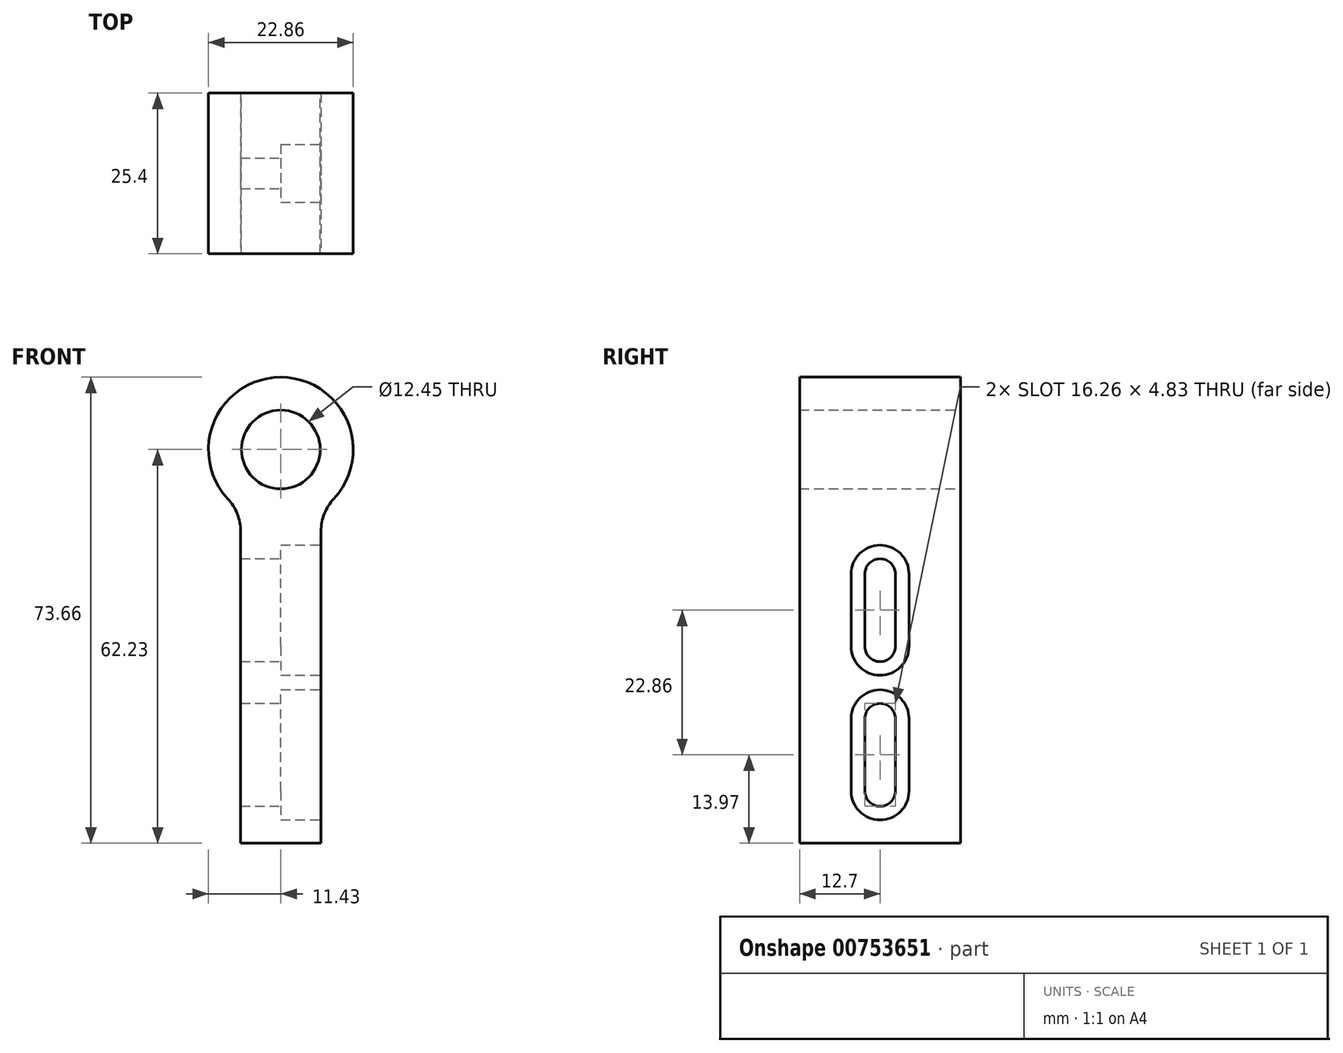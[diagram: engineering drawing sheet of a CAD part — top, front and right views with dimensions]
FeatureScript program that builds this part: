
annotation { "Feature Type Name" : "Feature", "Feature Type Description" : "" }
export const myFeature = defineFeature(function(context is Context, id is Id, definition is map)
    precondition{}
    {
        {
            var Q0;
            Q0=qCreatedBy(makeId("Front.planeOp"),FACE);
            var sketch = newSketch(context, id + "F0", { "sketchPlane" : qUnion([Q0])});
            skLineSegment(sketch, "E0", {"start": v(-6.35, 0) * mm, "end": v(6.35, 0) * mm});
            skLineSegment(sketch, "E1", {"start": v(6.35, 0) * mm, "end": v(6.35, 52.73) * mm});
            skLineSegment(sketch, "E2", {"start": v(-6.35, 52.73) * mm, "end": v(-6.35, 0) * mm});
            skCircle(sketch, "E3", {"center": v(0, 62.23) * mm, "radius": 6.22 * mm});
            skArc(sketch, "E4", {"start": v(6.35, 52.73) * mm, "mid": v(0, 73.66) * mm, "end": v(-6.35, 52.73) * mm});
            skSolve(sketch);
        }
        {
            var Q0;
            Q0=qSketchRegion(id+"F0",true);
            extrude(context, id + "F1", {"entities" : qUnion([Q0]), "endBound" : BoundingType.SYMMETRIC, "depth" : 25.4 * mm, "offsetDistance" : 25.4 * mm});
        }
        {
            var Q0;
            Q0=makeQuery(id+"F1.opExtrude","SWEPT_FACE",FACE,{"disambiguationData":[OSD([sQuery(id+"F0.wireOp",EDGE,"E1")])]});
            var sketch = newSketch(context, id + "F2", { "sketchPlane" : qUnion([Q0])});
            skCircle(sketch, "E5", {"center": v(0, 36.83) * mm, "radius": 2.41 * mm});
            skCircle(sketch, "E6", {"center": v(0, 13.97) * mm, "radius": 2.41 * mm});
            skSolve(sketch);
        }
        {
            var Q0;
            Q0=makeQuery(id+"F1.opExtrude","SWEPT_EDGE",EDGE,{"disambiguationData":[OSD([sQuery(id+"F0.wireOp",EDGE,"E2"),sQuery(id+"F0.wireOp",EDGE,"E4")])]});
            var Q1;
            {var subQ0=sQuery(id+"F0.wireOp",EDGE,"E2");Q1=makeQuery(id+"FnLNvNWXCwf8mwK_1.opChamfer","BLEND_EDGE",EDGE,{"blendedFrom":[makeQuery(id+"F1.opExtrude","SWEPT_EDGE",EDGE,{"disambiguationData":[OSD([subQ0,sQuery(id+"F0.wireOp",EDGE,"IJwo5JKE-T8f8-y26V-TljT-IEOYuoyi1ZoW")])]}),makeQuery(id+"F1.opExtrude","SWEPT_FACE",FACE,{"disambiguationData":[OSD([subQ0])]})],"blendedInto":[makeQuery(id+"F1.opExtrude","SWEPT_FACE",FACE,{"disambiguationData":[OSD([subQ0])]})]});}
            var Q2;
            {var subQ0=sQuery(id+"F0.wireOp",EDGE,"IJwo5JKE-T8f8-y26V-TljT-IEOYuoyi1ZoW");Q2=makeQuery(id+"FnLNvNWXCwf8mwK_1.opChamfer","BLEND_EDGE",EDGE,{"blendedFrom":[makeQuery(id+"F1.opExtrude","SWEPT_EDGE",EDGE,{"disambiguationData":[OSD([sQuery(id+"F0.wireOp",EDGE,"E2"),subQ0])]}),makeQuery(id+"F1.opExtrude","SWEPT_FACE",FACE,{"disambiguationData":[OSD([subQ0])]})],"blendedInto":[makeQuery(id+"F1.opExtrude","SWEPT_FACE",FACE,{"disambiguationData":[OSD([subQ0])]})]});}
            var Q3;
            {var subQ0=sQuery(id+"F0.wireOp",EDGE,"ahlNWd82-LXwS-C29I-S3m9-z0gpT5bYHWY6");Q3=makeQuery(id+"FnLNvNWXCwf8mwK_1.opChamfer","BLEND_EDGE",EDGE,{"blendedFrom":[makeQuery(id+"F1.opExtrude","SWEPT_EDGE",EDGE,{"disambiguationData":[OSD([sQuery(id+"F0.wireOp",EDGE,"E1"),subQ0])]}),makeQuery(id+"F1.opExtrude","SWEPT_FACE",FACE,{"disambiguationData":[OSD([subQ0])]})],"blendedInto":[makeQuery(id+"F1.opExtrude","SWEPT_FACE",FACE,{"disambiguationData":[OSD([subQ0])]})]});}
            var Q4;
            {var subQ0=sQuery(id+"F0.wireOp",EDGE,"E1");Q4=makeQuery(id+"FnLNvNWXCwf8mwK_1.opChamfer","BLEND_EDGE",EDGE,{"blendedFrom":[makeQuery(id+"F1.opExtrude","SWEPT_EDGE",EDGE,{"disambiguationData":[OSD([subQ0,sQuery(id+"F0.wireOp",EDGE,"ahlNWd82-LXwS-C29I-S3m9-z0gpT5bYHWY6")])]}),makeQuery(id+"F1.opExtrude","SWEPT_FACE",FACE,{"disambiguationData":[OSD([subQ0])]})],"blendedInto":[makeQuery(id+"F1.opExtrude","SWEPT_FACE",FACE,{"disambiguationData":[OSD([subQ0])]})]});}
            var Q5;
            Q5=makeQuery(id+"F1.opExtrude","SWEPT_EDGE",EDGE,{"disambiguationData":[OSD([sQuery(id+"F0.wireOp",EDGE,"E1"),sQuery(id+"F0.wireOp",EDGE,"E4")])]});
            fillet(context, id + "F3", {"entities" : qUnion([Q0, Q1, Q2, Q3, Q4, Q5]), "tangentPropagation" : true, "radius" : 7.62 * mm, "defaultsChanged" : true, "vertexSettings" : [], "allowEdgeOverflow" : false});
        }
        {
            var Q0;
            Q0=qSketchRegion(id+"F2",true);
            extrude(context, id + "F4", {"entities" : qUnion([Q0]), "operationType" : NewBodyOperationType.REMOVE, "endBound" : BoundingType.THROUGH_ALL, "oppositeDirection" : true, "depth" : 25.4 * mm, "offsetDistance" : 25.4 * mm});
        }
        {
            var Q0;
            Q0=makeQuery(id+"F1.opExtrude","SWEPT_FACE",FACE,{"disambiguationData":[OSD([sQuery(id+"F0.wireOp",EDGE,"E1")])]});
            var sketch = newSketch(context, id + "F5", { "sketchPlane" : qUnion([Q0])});
            skLineSegment(sketch, "E7.left", {"start": v(-2.41, 42.54) * mm, "end": v(-2.41, 31.12) * mm});
            skLineSegment(sketch, "E7.right", {"start": v(2.41, 42.54) * mm, "end": v(2.41, 31.12) * mm});
            skLineSegment(sketch, "E8.left", {"start": v(-2.41, 19.69) * mm, "end": v(-2.41, 8.26) * mm});
            skLineSegment(sketch, "E8.right", {"start": v(2.41, 19.69) * mm, "end": v(2.41, 8.26) * mm});
            skLineSegment(sketch, "E9", {"start": v(0, 36.83) * mm, "end": v(12.7, 36.83) * mm, "construction": true});
            skLineSegment(sketch, "E10", {"start": v(0, 13.97) * mm, "end": v(12.7, 13.97) * mm, "construction": true});
            skArc(sketch, "E11", {"start": v(2.41, 42.54) * mm, "mid": v(0, 44.96) * mm, "end": v(-2.41, 42.54) * mm});
            skArc(sketch, "E12", {"start": v(-2.41, 31.12) * mm, "mid": v(0, 28.7) * mm, "end": v(2.41, 31.12) * mm});
            skArc(sketch, "E13", {"start": v(2.41, 19.69) * mm, "mid": v(0, 22.1) * mm, "end": v(-2.41, 19.69) * mm});
            skArc(sketch, "E14", {"start": v(-2.41, 8.26) * mm, "mid": v(0, 5.84) * mm, "end": v(2.41, 8.26) * mm});
            skSolve(sketch);
        }
        {
            var Q0;
            Q0 = qSketchRegion(id + "F5", true);
            extrude(context, id + "F6", {"entities" : qUnion([Q0]), "operationType" : NewBodyOperationType.REMOVE, "endBound" : BoundingType.THROUGH_ALL, "oppositeDirection" : true, "depth" : 25.4 * mm, "offsetDistance" : 25.4 * mm});
        }
        {
            var Q0;
            Q0=makeQuery(id+"F1.opExtrude","SWEPT_FACE",FACE,{"disambiguationData":[OSD([sQuery(id+"F0.wireOp",EDGE,"E1")])]});
            var sketch = newSketch(context, id + "F7", { "sketchPlane" : qUnion([Q0])});
            skArc(sketch, "E15", {"start": v(4.57, 42.54) * mm, "mid": v(0, 47.12) * mm, "end": v(-4.57, 42.54) * mm});
            skArc(sketch, "E16", {"start": v(4.57, 19.69) * mm, "mid": v(0, 24.26) * mm, "end": v(-4.57, 19.69) * mm});
            skArc(sketch, "E17", {"start": v(-4.57, 31.12) * mm, "mid": v(0, 26.54) * mm, "end": v(4.57, 31.12) * mm});
            skArc(sketch, "E18", {"start": v(-4.57, 8.26) * mm, "mid": v(0, 3.68) * mm, "end": v(4.57, 8.26) * mm});
            skLineSegment(sketch, "E19", {"start": v(-4.57, 42.54) * mm, "end": v(-4.57, 31.12) * mm});
            skLineSegment(sketch, "E20", {"start": v(4.57, 42.54) * mm, "end": v(4.57, 31.12) * mm});
            skLineSegment(sketch, "E21", {"start": v(-4.57, 19.69) * mm, "end": v(-4.57, 8.26) * mm});
            skLineSegment(sketch, "E22", {"start": v(4.57, 19.69) * mm, "end": v(4.57, 8.26) * mm});
            skSolve(sketch);
        }
        {
            var Q0;
            Q0=qSketchRegion(id+"F7",true);
            extrude(context, id + "F8", {"entities" : qUnion([Q0]), "operationType" : NewBodyOperationType.REMOVE, "oppositeDirection" : true, "depth" : 6.35 * mm, "offsetDistance" : 25.4 * mm, "hasSecondDirection" : true, "secondDirectionBound" : SecondDirectionBoundingType.THROUGH_ALL, "secondDirectionOppositeDirection" : false, "secondDirectionDepth" : 25.4 * mm});
        }
    });
